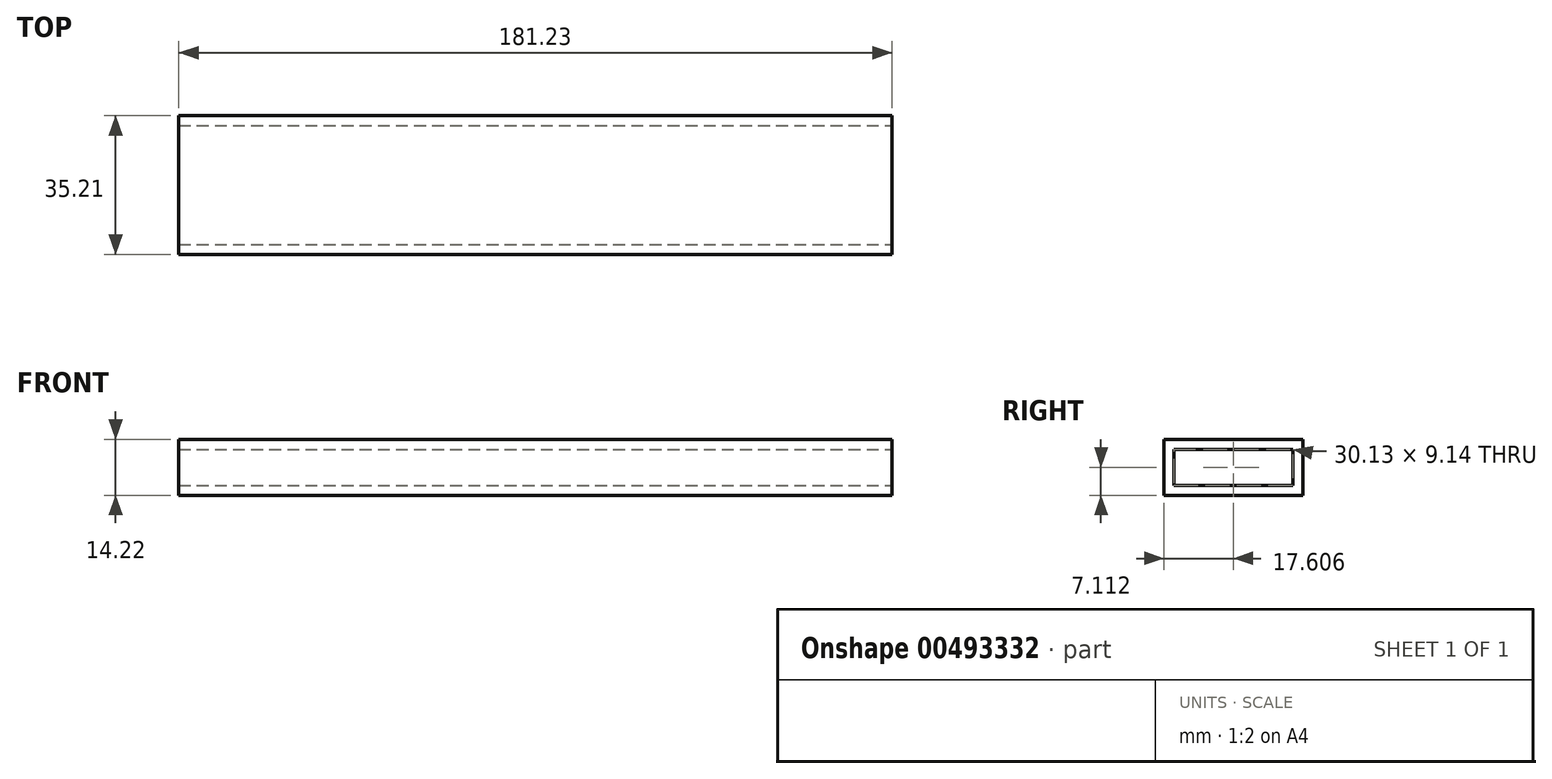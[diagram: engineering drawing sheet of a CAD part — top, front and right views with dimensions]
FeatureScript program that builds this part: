
annotation { "Feature Type Name" : "Feature", "Feature Type Description" : "" }
export const myFeature = defineFeature(function(context is Context, id is Id, definition is map)
    precondition{}
    {
        {
            var Q0;
            Q0=qCreatedBy(makeId("Top.planeOp"),FACE);
            var sketch = newSketch(context, id + "F0", { "sketchPlane" : qUnion([Q0])});
            skLineSegment(sketch, "E0.bottom", {"start": v(-91.67, 47.42) * mm, "end": v(89.56, 47.42) * mm});
            skLineSegment(sketch, "E0.top", {"start": v(-91.67, 12.2) * mm, "end": v(89.56, 12.2) * mm});
            skLineSegment(sketch, "E0.left", {"start": v(-91.67, 47.42) * mm, "end": v(-91.67, 12.2) * mm});
            skLineSegment(sketch, "E0.right", {"start": v(89.56, 47.42) * mm, "end": v(89.56, 12.2) * mm});
            skSolve(sketch);
        }
        {
            var Q0;
            Q0 = qSketchRegion(id + "F0", true);
            extrude(context, id + "F1", {"entities" : qUnion([Q0]), "depth" : 14.22 * mm});
        }
        {
            var Q0;
            Q0=makeQuery(id+"F1.opExtrude","SWEPT_FACE",FACE,{"disambiguationData":[OSD([sQuery(id+"F0.wireOp",EDGE,"E0.left")])]});
            var Q1;
            Q1=makeQuery(id+"F1.opExtrude","SWEPT_FACE",FACE,{"disambiguationData":[OSD([sQuery(id+"F0.wireOp",EDGE,"E0.right")])]});
            shell(context, id + "F2", {"entities" : qUnion([Q0, Q1]), "thickness" : 2.54 * mm});
        }
    });
